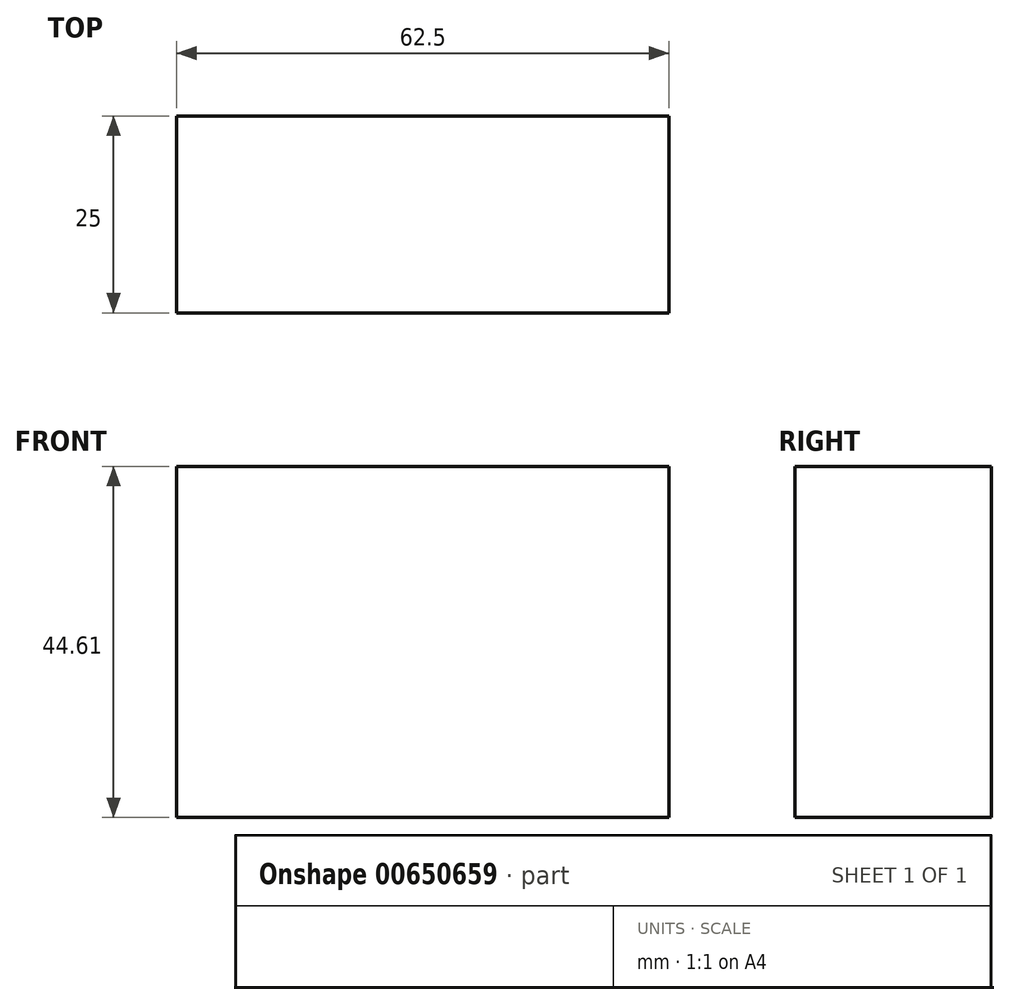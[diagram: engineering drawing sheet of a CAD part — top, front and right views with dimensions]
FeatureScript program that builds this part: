
annotation { "Feature Type Name" : "Feature", "Feature Type Description" : "" }
export const myFeature = defineFeature(function(context is Context, id is Id, definition is map)
    precondition{}
    {
        {
            var Q0;
            Q0=qCreatedBy(makeId("Front.planeOp"),FACE);
            var sketch = newSketch(context, id + "F0", { "sketchPlane" : qUnion([Q0])});
            skLineSegment(sketch, "E0.bottom", {"start": v(-33.56, 24.42) * mm, "end": v(28.94, 24.42) * mm});
            skLineSegment(sketch, "E0.top", {"start": v(-33.56, -20.2) * mm, "end": v(28.94, -20.2) * mm});
            skLineSegment(sketch, "E0.left", {"start": v(-33.56, 24.42) * mm, "end": v(-33.56, -20.2) * mm});
            skLineSegment(sketch, "E0.right", {"start": v(28.94, 24.42) * mm, "end": v(28.94, -20.2) * mm});
            skSolve(sketch);
        }
        {
            var Q0;
            Q0 = qSketchRegion(id + "F0", true);
            extrude(context, id + "F1", {"entities" : qUnion([Q0]), "depth" : 25 * mm, "offsetDistance" : 25 * mm});
        }
    });
